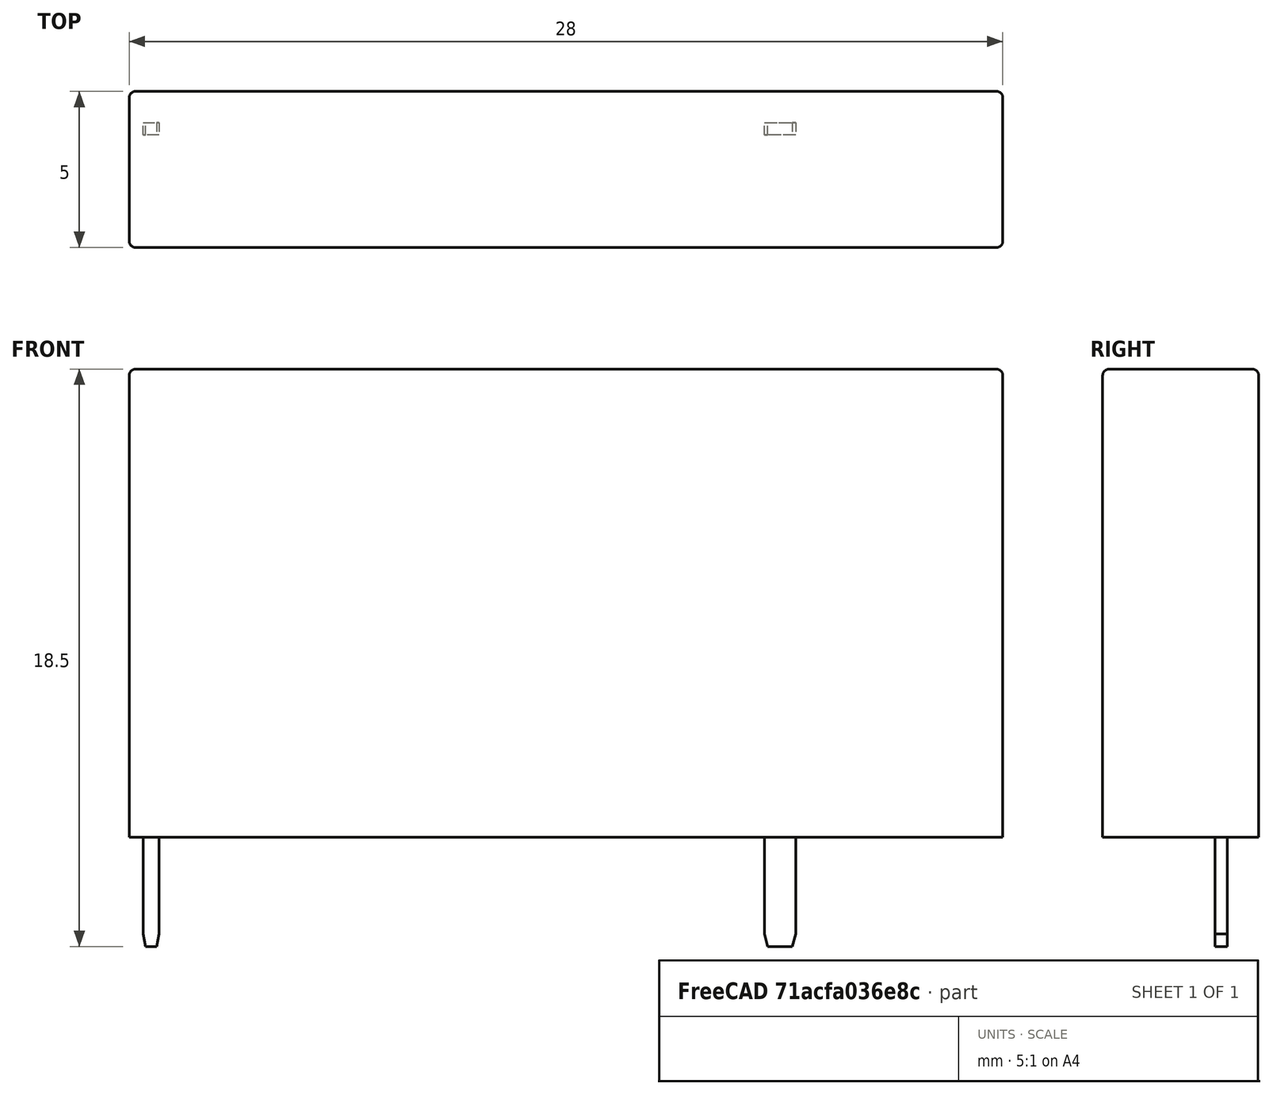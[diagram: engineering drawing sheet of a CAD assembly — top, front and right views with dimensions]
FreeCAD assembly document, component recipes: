
FREECAD ASSEMBLY — COMPONENT RECIPES ("FTR-LY_Cxxx")

This assembly document has 4 components, labeled P0..P3 below (a component is one placed body or linked part). 4 of them carry a construction recipe — the FreeCAD feature program that regenerates the part from scratch, quoted from this document or its linked companion documents; the rest are supplied as boundary geometry only. No exploded tour is included for this assembly.
COMPONENT P0 — recipe-attached ("Gehaeuse", modeled in this document).
Construction recipe (the document's own serialized feature program — sketch geometry with constraints, then the solid features built on it; lengths are millimeters unless a unit is written):

FEATURE [Sketcher::SketchObject] Sketch
  MapMode = 5
  Support = -> [XY_Plane]
  sketch-geometry (4):
    g0: LineSegment StartX=7.14 StartY=-3.8 StartZ=0 EndX=-20.86 EndY=-3.8 EndZ=0
    g1: LineSegment StartX=-20.86 StartY=-3.8 StartZ=0 EndX=-20.86 EndY=1.2 EndZ=0
    g2: LineSegment StartX=-20.86 StartY=1.2 StartZ=0 EndX=7.14 EndY=1.2 EndZ=0
    g3: LineSegment StartX=7.14 StartY=1.2 StartZ=0 EndX=7.14 EndY=-3.8 EndZ=0
  constraints (12):
    c: Coincident(g0,g1)
    c: Coincident(g1,g2)
    c: Coincident(g2,g3)
    c: Coincident(g3,g0)
    c: Horizontal(g0)
    c: Horizontal(g2)
    c: Vertical(g1)
    c: Vertical(g3)
    c: DistanceX(g2,g2) = 28
    c: DistanceY(g3,g3) = 5
    c: DistanceX(g-1,g2) = 7.14
    c: DistanceY(g-1,g2) = 1.2
FEATURE [PartDesign::Pad] Pad
  Length = 15
  Length2 = 100
  Profile = -> Sketch
  Type = 0
FEATURE [PartDesign::Fillet] Fillet
  Base = -> Pad [Edge1,Edge4,Edge12,Edge10,Edge8,Edge5,Edge2,Edge7]
  BaseFeature = -> Pad
  Radius = 0.2
  SupportTransform = true
FEATURE [PartDesign::Body] Body  label="Gehaeuse"
  Group = -> [Sketch,Pad,Fillet]
  Origin = -> Origin
  Tip = -> Fillet
COMPONENT P1 — recipe-attached ("Pin 14", modeled in this document).
Construction recipe (the document's own serialized feature program — sketch geometry with constraints, then the solid features built on it; lengths are millimeters unless a unit is written):

FEATURE [Sketcher::SketchObject] Sketch001
  MapMode = 5
  Support = -> [XY_Plane001]
  sketch-geometry (4):
    g0: LineSegment StartX=-0.5 StartY=0.2 StartZ=0 EndX=0.5 EndY=0.2 EndZ=0
    g1: LineSegment StartX=0.5 StartY=0.2 StartZ=0 EndX=0.5 EndY=-0.2 EndZ=0
    g2: LineSegment StartX=0.5 StartY=-0.2 StartZ=0 EndX=-0.5 EndY=-0.2 EndZ=0
    g3: LineSegment StartX=-0.5 StartY=-0.2 StartZ=0 EndX=-0.5 EndY=0.2 EndZ=0
  constraints (10):
    c: Coincident(g0,g1)
    c: Coincident(g1,g2)
    c: Coincident(g2,g3)
    c: Coincident(g3,g0)
    c: Horizontal(g2)
    c: Vertical(g3)
    c: DistanceX(g0,g0) = 1
    c: DistanceY(g1,g1) = 0.4
    c: Symmetric(g0,g0,g-2)
    c: Symmetric(g0,g1,g-1)
FEATURE [PartDesign::Pad] Pad001
  Length = 3.5
  Length2 = 100
  Profile = -> Sketch001
  Reversed = true
  Type = 0
FEATURE [PartDesign::Chamfer] Chamfer
  Angle = 15
  Base = -> Pad001 [Edge12,Edge7]
  BaseFeature = -> Pad001
  Size = 0.4
  SupportTransform = true
FEATURE [PartDesign::Body] Body001  label="Pin 11"
  Group = -> [Sketch001,Pad001,Chamfer]
  Origin = -> Origin001
  Tip = -> Chamfer
COMPONENT P2 — same part as P1; its construction recipe is shown at P1.
COMPONENT P3 — recipe-attached ("Pin A2", modeled in this document).
Construction recipe (the document's own serialized feature program — sketch geometry with constraints, then the solid features built on it; lengths are millimeters unless a unit is written):

FEATURE [Sketcher::SketchObject] Sketch002
  MapMode = 5
  Support = -> [XY_Plane002]
  sketch-geometry (4):
    g0: LineSegment StartX=-0.25 StartY=0.2 StartZ=0 EndX=0.25 EndY=0.2 EndZ=0
    g1: LineSegment StartX=0.25 StartY=0.2 StartZ=0 EndX=0.25 EndY=-0.2 EndZ=0
    g2: LineSegment StartX=0.25 StartY=-0.2 StartZ=0 EndX=-0.25 EndY=-0.2 EndZ=0
    g3: LineSegment StartX=-0.25 StartY=-0.2 StartZ=0 EndX=-0.25 EndY=0.2 EndZ=0
  constraints (10):
    c: Coincident(g0,g1)
    c: Coincident(g1,g2)
    c: Coincident(g2,g3)
    c: Coincident(g3,g0)
    c: Horizontal(g2)
    c: Vertical(g3)
    c: DistanceX(g0,g0) = 0.5
    c: DistanceY(g1,g1) = 0.4
    c: Symmetric(g0,g0,g-2)
    c: Symmetric(g0,g1,g-1)
FEATURE [PartDesign::Pad] Pad002
  Length = 3.5
  Length2 = 100
  Profile = -> Sketch002
  Reversed = true
  Type = 0
FEATURE [PartDesign::Chamfer] Chamfer001
  Angle = 10
  Base = -> Pad002 [Edge7,Edge12]
  BaseFeature = -> Pad002
  Size = 0.4
  SupportTransform = true
FEATURE [PartDesign::Body] Body002  label="Pin A1"
  Group = -> [Sketch002,Pad002,Chamfer001]
  Origin = -> Origin002
  Placement = pos=(-20.16,0,0) rot=(0,0,1;0rad)
  Tip = -> Chamfer001
PROVENANCE & LICENSES
A FreeCAD (.FCStd) document from a public repository crawl; recipes are the document's own serialized feature recipes (and, for linked parts, companion documents' recipes).
License: as declared in the source repository (recorded in the dataset sidecar).
